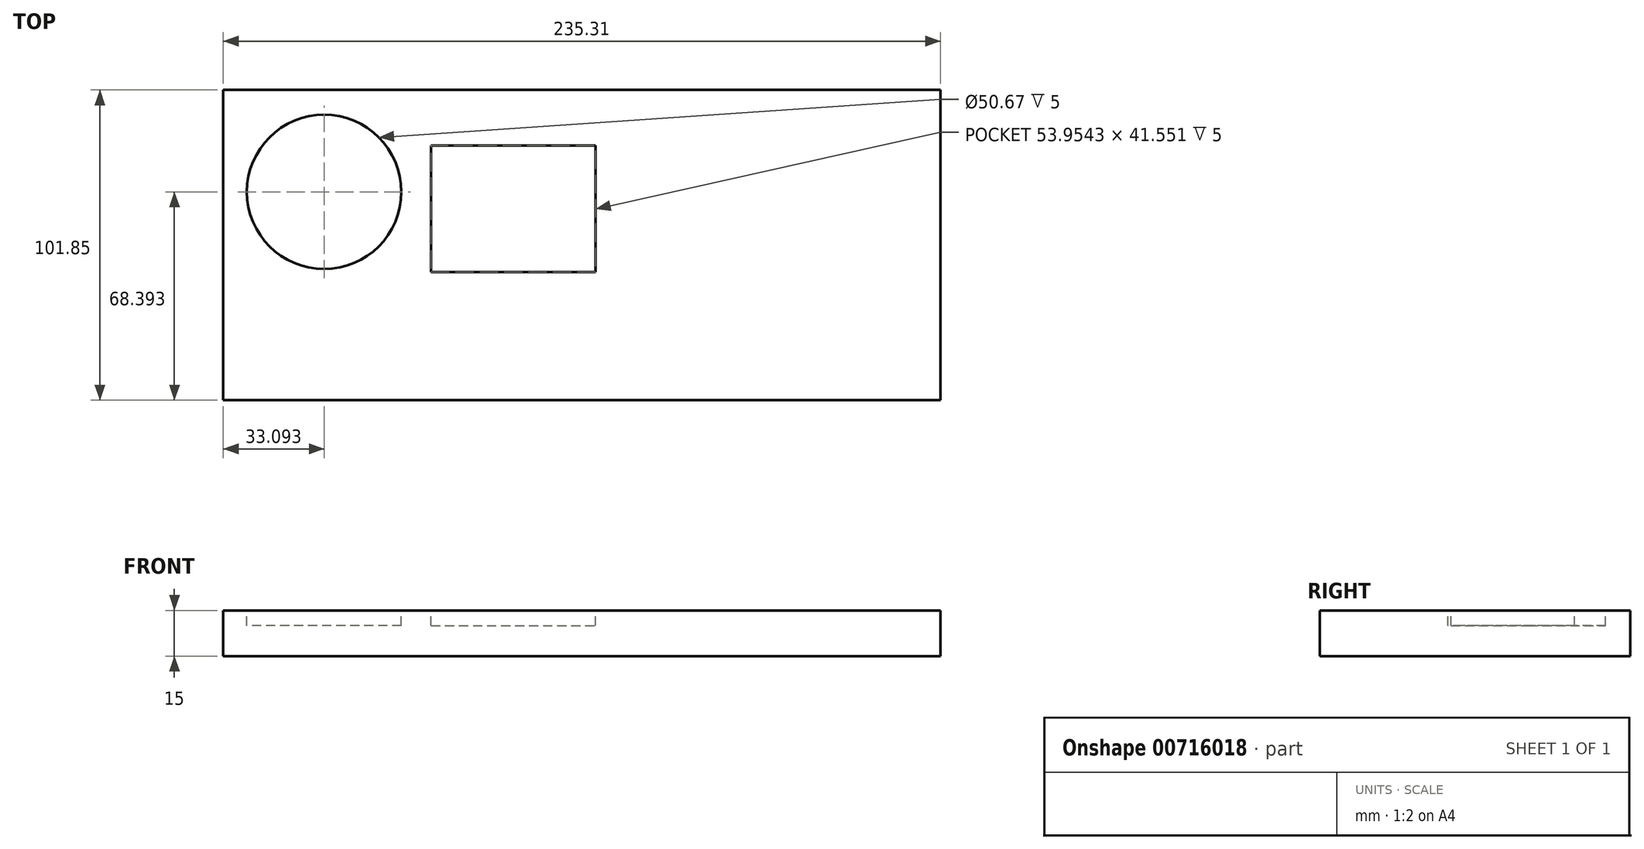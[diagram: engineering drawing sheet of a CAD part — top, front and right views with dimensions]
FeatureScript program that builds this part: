
annotation { "Feature Type Name" : "Feature", "Feature Type Description" : "" }
export const myFeature = defineFeature(function(context is Context, id is Id, definition is map)
    precondition{}
    {
        {
            var Q0;
            Q0=qCreatedBy(makeId("Top.planeOp"),FACE);
            var sketch = newSketch(context, id + "F0", { "sketchPlane" : qUnion([Q0])});
            skLineSegment(sketch, "E0.bottom", {"start": v(0, 1.8) * mm, "end": v(235.3, 1.8) * mm});
            skLineSegment(sketch, "E0.top", {"start": v(0, 103.65) * mm, "end": v(235.3, 103.65) * mm});
            skLineSegment(sketch, "E0.left", {"start": v(0, 1.8) * mm, "end": v(0, 103.65) * mm});
            skLineSegment(sketch, "E0.right", {"start": v(235.3, 1.8) * mm, "end": v(235.3, 103.65) * mm});
            skSolve(sketch);
        }
        {
            var Q0;
            Q0=makeQuery(id+"F0.imprint","IMPRINT",FACE,{"disambiguationData":[TD([[makeQuery(id+"F0.imprint","IMPRINT",EDGE,{"derivedFrom":sQuery(id+"F0.wireOp",EDGE,"E0.bottom")}),1.0]])]});
            extrude(context, id + "F1", {"entities" : qUnion([Q0]), "depth" : 15 * mm, "offsetDistance" : 25 * mm});
        }
        {
            var Q0;
            Q0=makeQuery(id+"F1.opExtrude","CAP_FACE",FACE,{"disambiguationData":[OSD([sQuery(id+"F0.wireOp",EDGE,"E0.bottom"),sQuery(id+"F0.wireOp",EDGE,"E0.top"),sQuery(id+"F0.wireOp",EDGE,"E0.left"),sQuery(id+"F0.wireOp",EDGE,"E0.right")])],"isStart":false});
            var sketch = newSketch(context, id + "F2", { "sketchPlane" : qUnion([Q0])});
            skCircle(sketch, "E1", {"center": v(33.1, 70.2) * mm, "radius": 25.34 * mm});
            skSolve(sketch);
        }
        {
            var Q0;
            Q0=makeQuery(id+"F2.imprint","IMPRINT",FACE,{"disambiguationData":[TD([[makeQuery(id+"F2.imprint","IMPRINT",EDGE,{"derivedFrom":sQuery(id+"F2.wireOp",EDGE,"E1")}),1.0]])]});
            extrude(context, id + "F3", {"entities" : qUnion([Q0]), "operationType" : NewBodyOperationType.REMOVE, "oppositeDirection" : true, "depth" : 5 * mm, "offsetDistance" : 25 * mm});
        }
        {
            var Q0;
            Q0=makeQuery(id+"F1.opExtrude","CAP_FACE",FACE,{"disambiguationData":[OSD([sQuery(id+"F0.wireOp",EDGE,"E0.bottom"),sQuery(id+"F0.wireOp",EDGE,"E0.top"),sQuery(id+"F0.wireOp",EDGE,"E0.left"),sQuery(id+"F0.wireOp",EDGE,"E0.right")])],"isStart":false});
            var sketch = newSketch(context, id + "F4", { "sketchPlane" : qUnion([Q0])});
            skLineSegment(sketch, "E2.bottom", {"start": v(68.14, 85.36) * mm, "end": v(122.1, 85.36) * mm});
            skLineSegment(sketch, "E2.top", {"start": v(68.14, 43.8) * mm, "end": v(122.1, 43.8) * mm});
            skLineSegment(sketch, "E2.left", {"start": v(68.14, 85.36) * mm, "end": v(68.14, 43.8) * mm});
            skLineSegment(sketch, "E2.right", {"start": v(122.1, 85.36) * mm, "end": v(122.1, 43.8) * mm});
            skSolve(sketch);
        }
        {
            var Q0;
            Q0 = qSketchRegion(id + "F4", true);
            extrude(context, id + "F5", {"entities" : qUnion([Q0]), "operationType" : NewBodyOperationType.REMOVE, "oppositeDirection" : true, "depth" : 5 * mm, "offsetDistance" : 25 * mm});
        }
    });
